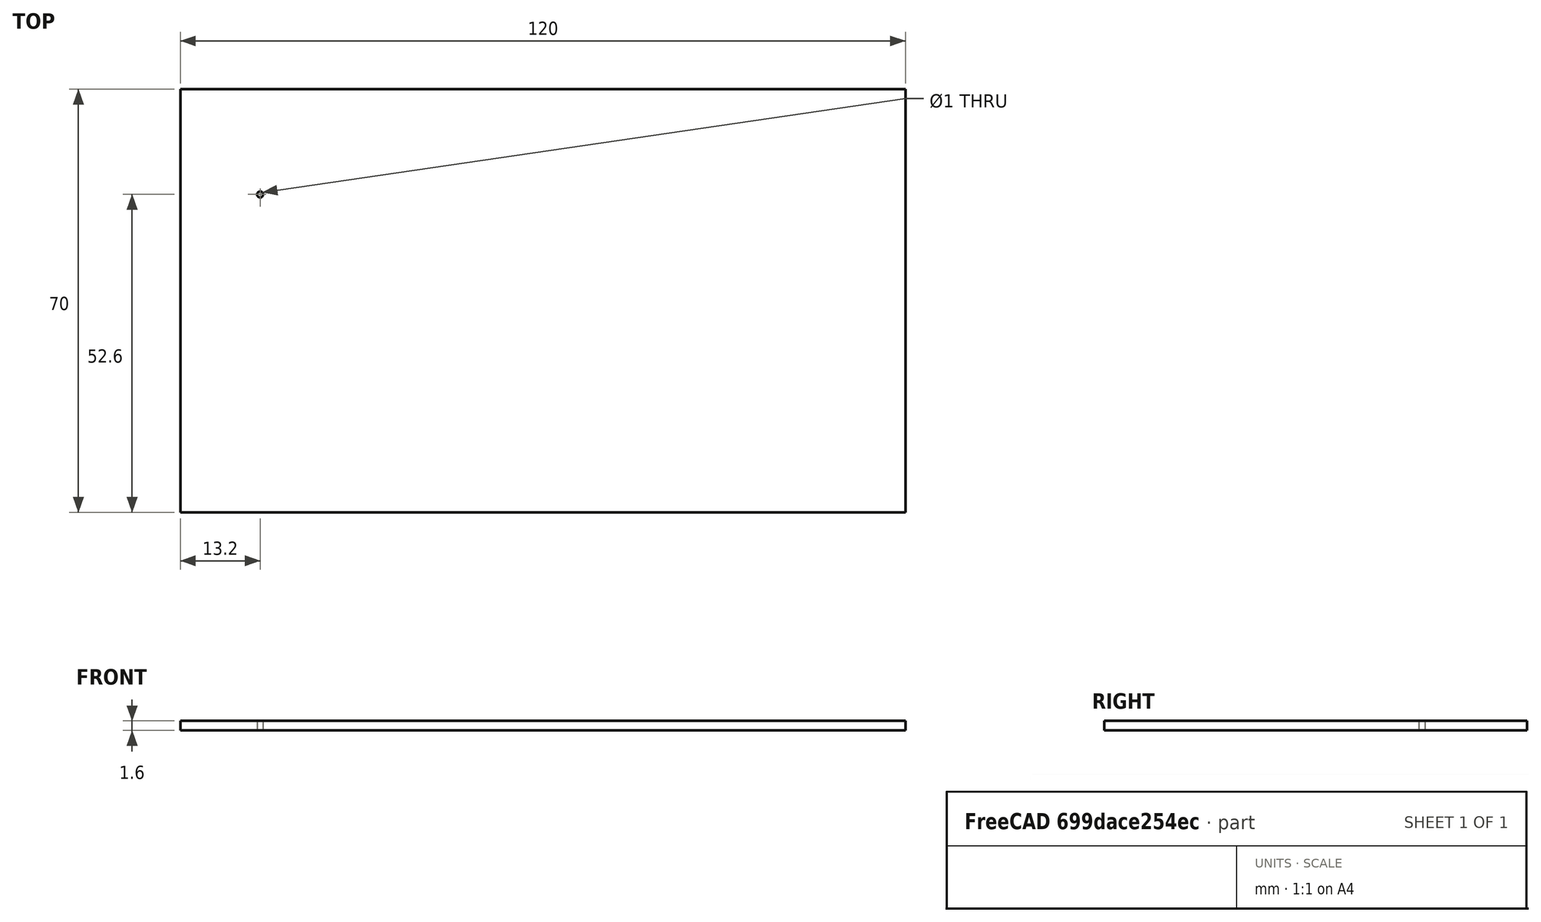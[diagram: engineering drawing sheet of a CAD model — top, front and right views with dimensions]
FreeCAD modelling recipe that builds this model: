
FCSTD DOCUMENT  (FreeCAD 0.19R22665 (Git))
Label: PCB-1.0
License: All rights reserved
LicenseURL: http://en.wikipedia.org/wiki/All_rights_reserved
objects: Sketcher::SketchObject×1, PartDesign::Pad×1, PartDesign::CoordinateSystem×1, PartDesign::Body×1
note: 5 computed .brp shape members not serialized (recipe doc carries the construction recipe); baked Part::Feature solids carry a one-line shape summary decoded from their .brp

FEATURE [Sketcher::SketchObject] Sketch001
  MapMode = 5
  Support = -> [XY_Plane]
  sketch-geometry (5):
    g0: LineSegment StartX=0 StartY=0 StartZ=0 EndX=120 EndY=0 EndZ=0
    g1: LineSegment StartX=120 StartY=0 StartZ=0 EndX=120 EndY=-70 EndZ=0
    g2: LineSegment StartX=120 StartY=-70 StartZ=0 EndX=0 EndY=-70 EndZ=0
    g3: LineSegment StartX=0 StartY=-70 StartZ=0 EndX=0 EndY=0 EndZ=0
    g4: Circle CenterX=13.2 CenterY=-17.4 CenterZ=0 NormalX=0 NormalY=0 NormalZ=1 AngleXU=0 Radius=0.5
  constraints (14):
    c: Coincident(g0,g1)
    c: Coincident(g1,g2)
    c: Coincident(g2,g3)
    c: Coincident(g3,g0)
    c: Horizontal(g0)
    c: Horizontal(g2)
    c: Vertical(g1)
    c: Vertical(g3)
    c: Coincident(g0,g-1)
    c: DistanceX(g0,g0) = 120
    c: DistanceY(g1,g1) = 70
    c: Diameter(g4) = 1
    c: DistanceX(g0,g4) = 13.2
    c: DistanceY(g4,g0) = 17.4
FEATURE [PartDesign::Pad] Pad
  Direction = (1,1,1)
  Length = 1.6
  Length2 = 100
  Profile = -> Sketch001
  Refine = true
  Type = 0
FEATURE [PartDesign::CoordinateSystem] LCS_1
  AttacherType = Attacher::AttachEngine3D
  MapMode = 11
  Placement = pos=(13.2,-17.4,0) rot=(0,0,1;1.5708rad)
  Support = -> [Pad]
FEATURE [PartDesign::Body] Body  label="PCB"
  Group = -> [Sketch001,Pad,LCS_1]
  Origin = -> Origin
  Tip = -> Pad
